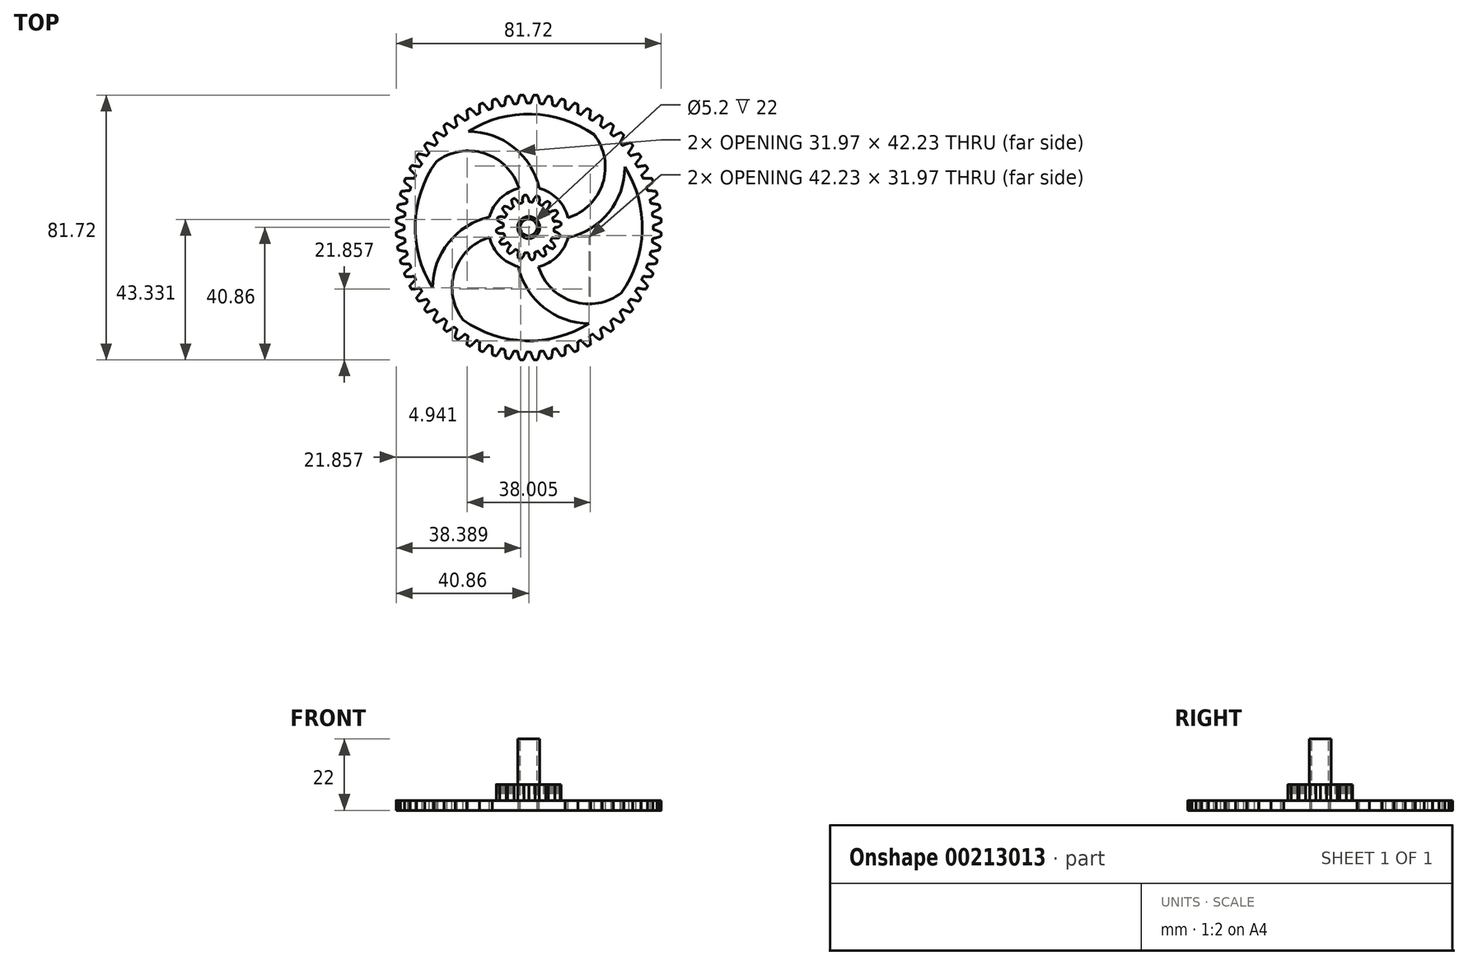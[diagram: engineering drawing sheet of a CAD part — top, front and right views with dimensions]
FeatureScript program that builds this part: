
annotation { "Feature Type Name" : "Feature", "Feature Type Description" : "" }
export const myFeature = defineFeature(function(context is Context, id is Id, definition is map)
    precondition{}
    {
        {
            var Q0;
            Q0=qCreatedBy(makeId("Top.planeOp"),FACE);
            var sketch = newSketch(context, id + "F0", { "sketchPlane" : qUnion([Q0])});
            skCircle(sketch, "E0", {"center": v(0, 0) * mm, "radius": 37.31 * mm, "construction": true});
            skLineSegment(sketch, "E1", {"start": v(0, 0) * mm, "end": v(37.31, 0) * mm, "construction": true});
            skLineSegment(sketch, "E2", {"start": v(37.31, 0) * mm, "end": v(37.31, 0) * mm});
            skLineSegment(sketch, "E3", {"start": v(0, 0) * mm, "end": v(37.27, 1.7) * mm, "construction": true});
            skLineSegment(sketch, "E4", {"start": v(37.27, 1.7) * mm, "end": v(37.35, 0) * mm, "construction": true});
            skLineSegment(sketch, "E5", {"start": v(0, 0) * mm, "end": v(37.16, 3.38) * mm, "construction": true});
            skLineSegment(sketch, "E6", {"start": v(37.16, 3.38) * mm, "end": v(37.46, 0) * mm, "construction": true});
            skLineSegment(sketch, "E7", {"start": v(0, 0) * mm, "end": v(36.97, 5.06) * mm, "construction": true});
            skLineSegment(sketch, "E8", {"start": v(36.97, 5.06) * mm, "end": v(37.66, 0.03) * mm, "construction": true});
            skLineSegment(sketch, "E9", {"start": v(0, 0) * mm, "end": v(36.7, 6.74) * mm, "construction": true});
            skLineSegment(sketch, "E10", {"start": v(36.7, 6.74) * mm, "end": v(37.92, 0.07) * mm, "construction": true});
            skLineSegment(sketch, "E11", {"start": v(0, 0) * mm, "end": v(36.36, 8.4) * mm, "construction": true});
            skLineSegment(sketch, "E12", {"start": v(36.36, 8.4) * mm, "end": v(38.26, 0.14) * mm, "construction": true});
            skLineSegment(sketch, "E13", {"start": v(0, 0) * mm, "end": v(35.94, 10.03) * mm, "construction": true});
            skLineSegment(sketch, "E14", {"start": v(35.94, 10.03) * mm, "end": v(38.67, 0.25) * mm, "construction": true});
            skLineSegment(sketch, "E15", {"start": v(0, 0) * mm, "end": v(35.44, 11.65) * mm, "construction": true});
            skLineSegment(sketch, "E16", {"start": v(35.44, 11.65) * mm, "end": v(39.15, 0.4) * mm, "construction": true});
            skLineSegment(sketch, "E17", {"start": v(0, 0) * mm, "end": v(34.88, 13.25) * mm, "construction": true});
            skLineSegment(sketch, "E18", {"start": v(34.88, 13.25) * mm, "end": v(39.69, 0.59) * mm, "construction": true});
            skLineSegment(sketch, "E19", {"start": v(0, 0) * mm, "end": v(34.24, 14.82) * mm, "construction": true});
            skLineSegment(sketch, "E20", {"start": v(34.24, 14.82) * mm, "end": v(40.3, 0.83) * mm, "construction": true});
            skLineSegment(sketch, "E21", {"start": v(0, 0) * mm, "end": v(33.54, 16.36) * mm, "construction": true});
            skLineSegment(sketch, "E22", {"start": v(33.54, 16.36) * mm, "end": v(40.96, 1.14) * mm, "construction": true});
            skPoint(sketch, "E23", {"position": v(37.31, 0) * mm});
            skCircle(sketch, "E24", {"center": v(0, 0) * mm, "radius": 38.38 * mm});
            skFitSpline(sketch, "E25", {"points": [v(37.31, 0) * mm, v(37.35, 0) * mm, v(37.46, 0) * mm, v(37.66, 0.03) * mm, v(37.92, 0.07) * mm, v(38.26, 0.14) * mm, v(38.67, 0.25) * mm, v(39.15, 0.4) * mm, v(39.69, 0.59) * mm, v(40.3, 0.83) * mm, v(40.96, 1.14) * mm], "startDerivative": vector(1, 0.02) * mm, "endDerivative": vector(4.58, 2.16) * mm, "construction": true});
            skFitSpline(sketch, "E26", {"points": [v(37.31, 0) * mm, v(37.35, 0) * mm, v(37.46, 0) * mm, v(37.66, 0.03) * mm, v(37.92, 0.07) * mm, v(38.26, 0.14) * mm, v(38.67, 0.25) * mm, v(39.15, 0.4) * mm, v(39.69, 0.59) * mm, v(40.3, 0.83) * mm, v(40.96, 1.14) * mm], "startDerivative": vector(1, 0.02) * mm, "endDerivative": vector(4.58, 2.16) * mm});
            skLineSegment(sketch, "E27", {"start": v(0, 0) * mm, "end": v(51.74, 2.13) * mm, "construction": true});
            skFitSpline(sketch, "E28.MirrorCS", {"points": [v(37.19, 3.06) * mm, v(37.22, 3.06) * mm, v(37.34, 3.07) * mm, v(37.53, 3.06) * mm, v(37.8, 3.04) * mm, v(38.14, 3) * mm, v(38.56, 2.93) * mm, v(39.05, 2.82) * mm, v(39.6, 2.67) * mm, v(40.23, 2.48) * mm, v(40.91, 2.23) * mm], "startDerivative": vector(1, 0.06) * mm, "endDerivative": vector(4.74, -1.78) * mm});
            skArc(sketch, "E29", {"start": v(40.83, 2.26) * mm, "mid": v(-40.86, -1.68) * mm, "end": v(40.88, 1.1) * mm, "construction": true});
            skArc(sketch, "E30", {"start": v(40.88, 1.1) * mm, "mid": v(40.86, 1.68) * mm, "end": v(40.83, 2.26) * mm});
            skSolve(sketch);
        }
        {
            var Q0;
            Q0=qCreatedBy(makeId("Front.planeOp"),FACE);
            var sketch = newSketch(context, id + "F1", { "sketchPlane" : qUnion([Q0])});
            skLineSegment(sketch, "E31", {"start": v(0, 0) * mm, "end": v(0, 52.01) * mm});
            skSolve(sketch);
        }
        {
            var Q0;
            {var subQ0=sQuery(id+"F0.wireOp",EDGE,"E24");var subQ1=makeQuery(id+"F0.imprint","INTERSECT",VERTEX,{"derivedFrom":[subQ0,sQuery(id+"F0.wireOp",EDGE,"E26")]});Q0=makeQuery(id+"F0.imprint","IMPRINT",FACE,{"disambiguationData":[TD([[makeQuery(id+"F0.imprint","IMPRINT",EDGE,{"disambiguationData":[TD([[subQ1,-1.0]])],"derivedFrom":subQ0}),1.0]])]});}
            var Q1;
            {var subQ0=sQuery(id+"F0.wireOp",EDGE,"E26");Q1=makeQuery(id+"F0.imprint","IMPRINT",FACE,{"disambiguationData":[TD([[makeQuery(id+"F0.imprint","IMPRINT",EDGE,{"derivedFrom":subQ0}),1.0]])]});}
            extrude(context, id + "F2", {"entities" : qUnion([Q0, Q1]), "depth" : 3 * mm});
        }
        {
            var Q0;
            Q0=makeQuery(id+"F2.opExtrude","SWEPT_EDGE",EDGE,{"disambiguationData":[OSD([sQuery(id+"F0.wireOp",EDGE,"E24"),sQuery(id+"F0.wireOp",EDGE,"E26")])]});
            var Q1;
            Q1=makeQuery(id+"F2.opExtrude","SWEPT_EDGE",EDGE,{"disambiguationData":[OSD([sQuery(id+"F0.wireOp",EDGE,"E26"),sQuery(id+"F0.wireOp",EDGE,"E30")])]});
            var Q2;
            Q2=makeQuery(id+"F2.opExtrude","SWEPT_EDGE",EDGE,{"disambiguationData":[OSD([sQuery(id+"F0.wireOp",EDGE,"E28.MirrorCS"),sQuery(id+"F0.wireOp",EDGE,"E30")])]});
            var Q3;
            Q3=makeQuery(id+"F2.opExtrude","SWEPT_EDGE",EDGE,{"disambiguationData":[OSD([sQuery(id+"F0.wireOp",EDGE,"E24"),sQuery(id+"F0.wireOp",EDGE,"E28.MirrorCS")])]});
            fillet(context, id + "F3", {"entities" : qUnion([Q0, Q1, Q2, Q3]), "radius" : 0.3 * mm, "tangentPropagation" : true, "allowEdgeOverflow" : false});
        }
        {
            var Q0;
            Q0=makeQuery(id+"F2.opExtrude","SWEPT_BODY",BODY,{"disambiguationData":[OSD([sQuery(id+"F0.wireOp",EDGE,"E24"),sQuery(id+"F0.wireOp",EDGE,"E26"),sQuery(id+"F0.wireOp",EDGE,"E28.MirrorCS"),sQuery(id+"F0.wireOp",EDGE,"E30")])]});
            var Q1;
            Q1=sQuery(id+"F1.wireOp",EDGE,"E31");
            circularPattern(context, id + "F4", {"operationType" : NewBodyOperationType.ADD, "entities" : qUnion([Q0]), "axis" : qUnion([Q1]), "angle" : 360 * degree, "instanceCount" : 60, "equalSpace" : true});
        }
        {
            var Q0;
            {var subQ0=makeQuery(id+"F2.opExtrude","CAP_FACE",FACE,{"disambiguationData":[OSD([sQuery(id+"F0.wireOp",EDGE,"E24"),sQuery(id+"F0.wireOp",EDGE,"E26"),sQuery(id+"F0.wireOp",EDGE,"E28.MirrorCS"),sQuery(id+"F0.wireOp",EDGE,"E30")])],"isStart":false});Q0=makeQuery(id+"F4.boolean.opBoolean","MERGE",FACE,{"derivedFrom":[subQ0,makeQuery(id+"F4.opPattern","COPY",FACE,{"derivedFrom":subQ0,"instanceName":"1"}),makeQuery(id+"F4.opPattern","COPY",FACE,{"derivedFrom":subQ0,"instanceName":"2"}),makeQuery(id+"F4.opPattern","COPY",FACE,{"derivedFrom":subQ0,"instanceName":"3"}),makeQuery(id+"F4.opPattern","COPY",FACE,{"derivedFrom":subQ0,"instanceName":"4"}),makeQuery(id+"F4.opPattern","COPY",FACE,{"derivedFrom":subQ0,"instanceName":"5"}),makeQuery(id+"F4.opPattern","COPY",FACE,{"derivedFrom":subQ0,"instanceName":"6"}),makeQuery(id+"F4.opPattern","COPY",FACE,{"derivedFrom":subQ0,"instanceName":"7"}),makeQuery(id+"F4.opPattern","COPY",FACE,{"derivedFrom":subQ0,"instanceName":"8"}),makeQuery(id+"F4.opPattern","COPY",FACE,{"derivedFrom":subQ0,"instanceName":"9"}),makeQuery(id+"F4.opPattern","COPY",FACE,{"derivedFrom":subQ0,"instanceName":"10"}),makeQuery(id+"F4.opPattern","COPY",FACE,{"derivedFrom":subQ0,"instanceName":"11"}),makeQuery(id+"F4.opPattern","COPY",FACE,{"derivedFrom":subQ0,"instanceName":"12"}),makeQuery(id+"F4.opPattern","COPY",FACE,{"derivedFrom":subQ0,"instanceName":"13"}),makeQuery(id+"F4.opPattern","COPY",FACE,{"derivedFrom":subQ0,"instanceName":"14"}),makeQuery(id+"F4.opPattern","COPY",FACE,{"derivedFrom":subQ0,"instanceName":"15"}),makeQuery(id+"F4.opPattern","COPY",FACE,{"derivedFrom":subQ0,"instanceName":"16"}),makeQuery(id+"F4.opPattern","COPY",FACE,{"derivedFrom":subQ0,"instanceName":"17"}),makeQuery(id+"F4.opPattern","COPY",FACE,{"derivedFrom":subQ0,"instanceName":"18"}),makeQuery(id+"F4.opPattern","COPY",FACE,{"derivedFrom":subQ0,"instanceName":"19"}),makeQuery(id+"F4.opPattern","COPY",FACE,{"derivedFrom":subQ0,"instanceName":"20"}),makeQuery(id+"F4.opPattern","COPY",FACE,{"derivedFrom":subQ0,"instanceName":"21"}),makeQuery(id+"F4.opPattern","COPY",FACE,{"derivedFrom":subQ0,"instanceName":"22"}),makeQuery(id+"F4.opPattern","COPY",FACE,{"derivedFrom":subQ0,"instanceName":"23"}),makeQuery(id+"F4.opPattern","COPY",FACE,{"derivedFrom":subQ0,"instanceName":"24"}),makeQuery(id+"F4.opPattern","COPY",FACE,{"derivedFrom":subQ0,"instanceName":"25"}),makeQuery(id+"F4.opPattern","COPY",FACE,{"derivedFrom":subQ0,"instanceName":"26"}),makeQuery(id+"F4.opPattern","COPY",FACE,{"derivedFrom":subQ0,"instanceName":"27"}),makeQuery(id+"F4.opPattern","COPY",FACE,{"derivedFrom":subQ0,"instanceName":"28"}),makeQuery(id+"F4.opPattern","COPY",FACE,{"derivedFrom":subQ0,"instanceName":"29"}),makeQuery(id+"F4.opPattern","COPY",FACE,{"derivedFrom":subQ0,"instanceName":"30"}),makeQuery(id+"F4.opPattern","COPY",FACE,{"derivedFrom":subQ0,"instanceName":"31"}),makeQuery(id+"F4.opPattern","COPY",FACE,{"derivedFrom":subQ0,"instanceName":"32"}),makeQuery(id+"F4.opPattern","COPY",FACE,{"derivedFrom":subQ0,"instanceName":"33"}),makeQuery(id+"F4.opPattern","COPY",FACE,{"derivedFrom":subQ0,"instanceName":"34"}),makeQuery(id+"F4.opPattern","COPY",FACE,{"derivedFrom":subQ0,"instanceName":"35"}),makeQuery(id+"F4.opPattern","COPY",FACE,{"derivedFrom":subQ0,"instanceName":"36"}),makeQuery(id+"F4.opPattern","COPY",FACE,{"derivedFrom":subQ0,"instanceName":"37"}),makeQuery(id+"F4.opPattern","COPY",FACE,{"derivedFrom":subQ0,"instanceName":"38"}),makeQuery(id+"F4.opPattern","COPY",FACE,{"derivedFrom":subQ0,"instanceName":"39"}),makeQuery(id+"F4.opPattern","COPY",FACE,{"derivedFrom":subQ0,"instanceName":"40"}),makeQuery(id+"F4.opPattern","COPY",FACE,{"derivedFrom":subQ0,"instanceName":"41"}),makeQuery(id+"F4.opPattern","COPY",FACE,{"derivedFrom":subQ0,"instanceName":"42"}),makeQuery(id+"F4.opPattern","COPY",FACE,{"derivedFrom":subQ0,"instanceName":"43"}),makeQuery(id+"F4.opPattern","COPY",FACE,{"derivedFrom":subQ0,"instanceName":"44"}),makeQuery(id+"F4.opPattern","COPY",FACE,{"derivedFrom":subQ0,"instanceName":"45"}),makeQuery(id+"F4.opPattern","COPY",FACE,{"derivedFrom":subQ0,"instanceName":"46"}),makeQuery(id+"F4.opPattern","COPY",FACE,{"derivedFrom":subQ0,"instanceName":"47"}),makeQuery(id+"F4.opPattern","COPY",FACE,{"derivedFrom":subQ0,"instanceName":"48"}),makeQuery(id+"F4.opPattern","COPY",FACE,{"derivedFrom":subQ0,"instanceName":"49"}),makeQuery(id+"F4.opPattern","COPY",FACE,{"derivedFrom":subQ0,"instanceName":"50"}),makeQuery(id+"F4.opPattern","COPY",FACE,{"derivedFrom":subQ0,"instanceName":"51"}),makeQuery(id+"F4.opPattern","COPY",FACE,{"derivedFrom":subQ0,"instanceName":"52"}),makeQuery(id+"F4.opPattern","COPY",FACE,{"derivedFrom":subQ0,"instanceName":"53"}),makeQuery(id+"F4.opPattern","COPY",FACE,{"derivedFrom":subQ0,"instanceName":"54"}),makeQuery(id+"F4.opPattern","COPY",FACE,{"derivedFrom":subQ0,"instanceName":"55"}),makeQuery(id+"F4.opPattern","COPY",FACE,{"derivedFrom":subQ0,"instanceName":"56"}),makeQuery(id+"F4.opPattern","COPY",FACE,{"derivedFrom":subQ0,"instanceName":"57"}),makeQuery(id+"F4.opPattern","COPY",FACE,{"derivedFrom":subQ0,"instanceName":"58"}),makeQuery(id+"F4.opPattern","COPY",FACE,{"derivedFrom":subQ0,"instanceName":"59"})]});}
            var sketch = newSketch(context, id + "F5", { "sketchPlane" : qUnion([Q0])});
            skLineSegment(sketch, "E32", {"start": v(0, 0) * mm, "end": v(38.38, -0.43) * mm, "construction": true});
            skCircle(sketch, "E33", {"center": v(0, 0) * mm, "radius": 8.46 * mm, "construction": true});
            skLineSegment(sketch, "E34", {"start": v(7.68, 4.49) * mm, "end": v(7.68, 4.49) * mm});
            skLineSegment(sketch, "E35", {"start": v(0, 0) * mm, "end": v(8.44, 0.55) * mm, "construction": true});
            skLineSegment(sketch, "E36", {"start": v(8.44, 0.55) * mm, "end": v(8.47, 0) * mm, "construction": true});
            skLineSegment(sketch, "E37", {"start": v(0, 0) * mm, "end": v(8.39, 1.09) * mm, "construction": true});
            skLineSegment(sketch, "E38", {"start": v(8.39, 1.09) * mm, "end": v(8.53, 0) * mm, "construction": true});
            skLineSegment(sketch, "E39", {"start": v(0, 0) * mm, "end": v(8.3, 1.63) * mm, "construction": true});
            skLineSegment(sketch, "E40", {"start": v(8.3, 1.63) * mm, "end": v(8.61, 0.02) * mm, "construction": true});
            skLineSegment(sketch, "E41", {"start": v(0, 0) * mm, "end": v(8.18, 2.16) * mm, "construction": true});
            skLineSegment(sketch, "E42", {"start": v(8.18, 2.16) * mm, "end": v(8.73, 0.05) * mm, "construction": true});
            skLineSegment(sketch, "E43", {"start": v(0, 0) * mm, "end": v(8.02, 2.68) * mm, "construction": true});
            skLineSegment(sketch, "E44", {"start": v(8.02, 2.68) * mm, "end": v(8.89, 0.1) * mm, "construction": true});
            skLineSegment(sketch, "E45", {"start": v(0, 0) * mm, "end": v(7.83, 3.2) * mm, "construction": true});
            skLineSegment(sketch, "E46", {"start": v(7.83, 3.2) * mm, "end": v(9.07, 0.16) * mm, "construction": true});
            skLineSegment(sketch, "E47", {"start": v(0, 0) * mm, "end": v(7.6, 3.7) * mm, "construction": true});
            skLineSegment(sketch, "E48", {"start": v(7.6, 3.7) * mm, "end": v(9.28, 0.26) * mm, "construction": true});
            skLineSegment(sketch, "E49", {"start": v(0, 0) * mm, "end": v(7.35, 4.18) * mm, "construction": true});
            skLineSegment(sketch, "E50", {"start": v(7.35, 4.18) * mm, "end": v(9.51, 0.38) * mm, "construction": true});
            skLineSegment(sketch, "E51", {"start": v(0, 0) * mm, "end": v(7.07, 4.64) * mm, "construction": true});
            skLineSegment(sketch, "E52", {"start": v(7.07, 4.64) * mm, "end": v(9.77, 0.53) * mm, "construction": true});
            skLineSegment(sketch, "E53", {"start": v(0, 0) * mm, "end": v(6.75, 5.09) * mm, "construction": true});
            skLineSegment(sketch, "E54", {"start": v(6.75, 5.09) * mm, "end": v(10.04, 0.73) * mm, "construction": true});
            skPoint(sketch, "E55", {"position": v(8.46, 0) * mm});
            skCircle(sketch, "E56", {"center": v(0, 0) * mm, "radius": 7.87 * mm});
            skLineSegment(sketch, "E57", {"start": v(7.87, 0) * mm, "end": v(8.46, 0) * mm});
            skFitSpline(sketch, "E58", {"points": [v(8.46, 0) * mm, v(8.47, 0) * mm, v(8.53, 0) * mm, v(8.61, 0.02) * mm, v(8.73, 0.05) * mm, v(8.89, 0.1) * mm, v(9.07, 0.16) * mm, v(9.28, 0.26) * mm, v(9.51, 0.38) * mm, v(9.77, 0.53) * mm, v(10.04, 0.73) * mm], "startDerivative": vector(0.46, 0.01) * mm, "endDerivative": vector(1.88, 1.36) * mm});
            skFitSpline(sketch, "E59", {"points": [v(8.46, 0) * mm, v(8.47, 0) * mm, v(8.53, 0) * mm, v(8.61, 0.02) * mm, v(8.73, 0.05) * mm, v(8.89, 0.1) * mm, v(9.07, 0.16) * mm, v(9.28, 0.26) * mm, v(9.51, 0.38) * mm, v(9.77, 0.53) * mm, v(10.04, 0.73) * mm], "startDerivative": vector(0.46, 0.01) * mm, "endDerivative": vector(1.88, 1.36) * mm, "construction": true});
            skLineSegment(sketch, "E60", {"start": v(0, 0) * mm, "end": v(11.88, 1.35) * mm, "construction": true});
            skLineSegment(sketch, "E61.MirrorCS", {"start": v(7.67, 1.77) * mm, "end": v(8.24, 1.9) * mm});
            skFitSpline(sketch, "E62.MirrorCS", {"points": [v(8.24, 1.9) * mm, v(8.26, 1.9) * mm, v(8.31, 1.9) * mm, v(8.4, 1.91) * mm, v(8.52, 1.91) * mm, v(8.68, 1.9) * mm, v(8.87, 1.88) * mm, v(9.1, 1.83) * mm, v(9.35, 1.76) * mm, v(9.64, 1.67) * mm, v(9.95, 1.54) * mm], "startDerivative": vector(0.45, 0.1) * mm, "endDerivative": vector(2.14, -0.9) * mm});
            skArc(sketch, "E63", {"start": v(9.89, 1.57) * mm, "mid": v(-9.95, -1.13) * mm, "end": v(9.99, 0.7) * mm, "construction": true});
            skArc(sketch, "E64", {"start": v(9.99, 0.7) * mm, "mid": v(9.95, 1.13) * mm, "end": v(9.89, 1.57) * mm});
            skSolve(sketch);
        }
        {
            var Q0;
            Q0=makeQuery(id+"F2.opExtrude","SWEPT_BODY",BODY,{"disambiguationData":[OSD([sQuery(id+"F0.wireOp",EDGE,"E24"),sQuery(id+"F0.wireOp",EDGE,"E26"),sQuery(id+"F0.wireOp",EDGE,"E28.MirrorCS"),sQuery(id+"F0.wireOp",EDGE,"E30")])]});
            var Q1;
            Q1=sQuery(id+"F1.wireOp",EDGE,"E31");
            transform(context, id + "F6", {"entities" : qUnion([Q0]), "transformType" : TransformType.ROTATION, "transformAxis" : qUnion([Q1]), "angle" : 0.65 * degree, "makeCopy" : false});
        }
        {
            var Q0;
            {var subQ0=sQuery(id+"F5.wireOp",EDGE,"E56");var subQ1=makeQuery(id+"F5.imprint","INTERSECT",VERTEX,{"derivedFrom":[subQ0,sQuery(id+"F5.wireOp",EDGE,"E57")]});Q0=makeQuery(id+"F5.imprint","IMPRINT",FACE,{"disambiguationData":[TD([[makeQuery(id+"F5.imprint","IMPRINT",EDGE,{"disambiguationData":[TD([[subQ1,-1.0]])],"derivedFrom":subQ0}),1.0]])]});}
            var Q1;
            {var subQ1=sQuery(id+"F5.wireOp",EDGE,"E57");Q1=makeQuery(id+"F5.imprint","IMPRINT",FACE,{"disambiguationData":[TD([[makeQuery(id+"F5.imprint","IMPRINT",EDGE,{"derivedFrom":subQ1}),1.0]])]});}
            extrude(context, id + "F7", {"entities" : qUnion([Q0, Q1]), "depth" : 5 * mm});
        }
        {
            var Q0;
            Q0=makeQuery(id+"F7.opExtrude","SWEPT_EDGE",EDGE,{"disambiguationData":[OSD([sQuery(id+"F5.wireOp",EDGE,"E56"),sQuery(id+"F5.wireOp",EDGE,"E57")])]});
            var Q1;
            Q1=makeQuery(id+"F7.opExtrude","SWEPT_EDGE",EDGE,{"disambiguationData":[OSD([sQuery(id+"F5.wireOp",EDGE,"E58"),sQuery(id+"F5.wireOp",EDGE,"E64")])]});
            var Q2;
            Q2=makeQuery(id+"F7.opExtrude","SWEPT_EDGE",EDGE,{"disambiguationData":[OSD([sQuery(id+"F5.wireOp",EDGE,"E62.MirrorCS"),sQuery(id+"F5.wireOp",EDGE,"E64")])]});
            var Q3;
            Q3=makeQuery(id+"F7.opExtrude","SWEPT_EDGE",EDGE,{"disambiguationData":[OSD([sQuery(id+"F5.wireOp",EDGE,"E56"),sQuery(id+"F5.wireOp",EDGE,"E61.MirrorCS")])]});
            fillet(context, id + "F8", {"entities" : qUnion([Q0, Q1, Q2, Q3]), "radius" : 0.3 * mm, "tangentPropagation" : true, "allowEdgeOverflow" : false});
        }
        {
            var Q0;
            Q0=makeQuery(id+"F7.opExtrude","SWEPT_BODY",BODY,{"disambiguationData":[OSD([sQuery(id+"F5.wireOp",EDGE,"E56"),sQuery(id+"F5.wireOp",EDGE,"E57"),sQuery(id+"F5.wireOp",EDGE,"E58"),sQuery(id+"F5.wireOp",EDGE,"E61.MirrorCS"),sQuery(id+"F5.wireOp",EDGE,"E62.MirrorCS"),sQuery(id+"F5.wireOp",EDGE,"E64")])]});
            var Q1;
            Q1=sQuery(id+"F1.wireOp",EDGE,"E31");
            circularPattern(context, id + "F9", {"operationType" : NewBodyOperationType.ADD, "entities" : qUnion([Q0]), "axis" : qUnion([Q1]), "angle" : 360 * degree, "instanceCount" : 16, "equalSpace" : true});
        }
        {
            var Q0;
            {var subQ0=makeQuery(id+"F7.opExtrude","CAP_FACE",FACE,{"disambiguationData":[OSD([sQuery(id+"F5.wireOp",EDGE,"E56"),sQuery(id+"F5.wireOp",EDGE,"E57"),sQuery(id+"F5.wireOp",EDGE,"E58"),sQuery(id+"F5.wireOp",EDGE,"E61.MirrorCS"),sQuery(id+"F5.wireOp",EDGE,"E62.MirrorCS"),sQuery(id+"F5.wireOp",EDGE,"E64")])],"isStart":false});Q0=makeQuery(id+"F9.boolean.opBoolean","MERGE",FACE,{"derivedFrom":[subQ0,makeQuery(id+"F9.opPattern","COPY",FACE,{"derivedFrom":subQ0,"instanceName":"1"}),makeQuery(id+"F9.opPattern","COPY",FACE,{"derivedFrom":subQ0,"instanceName":"2"}),makeQuery(id+"F9.opPattern","COPY",FACE,{"derivedFrom":subQ0,"instanceName":"3"}),makeQuery(id+"F9.opPattern","COPY",FACE,{"derivedFrom":subQ0,"instanceName":"4"}),makeQuery(id+"F9.opPattern","COPY",FACE,{"derivedFrom":subQ0,"instanceName":"5"}),makeQuery(id+"F9.opPattern","COPY",FACE,{"derivedFrom":subQ0,"instanceName":"6"}),makeQuery(id+"F9.opPattern","COPY",FACE,{"derivedFrom":subQ0,"instanceName":"7"}),makeQuery(id+"F9.opPattern","COPY",FACE,{"derivedFrom":subQ0,"instanceName":"8"}),makeQuery(id+"F9.opPattern","COPY",FACE,{"derivedFrom":subQ0,"instanceName":"9"}),makeQuery(id+"F9.opPattern","COPY",FACE,{"derivedFrom":subQ0,"instanceName":"10"}),makeQuery(id+"F9.opPattern","COPY",FACE,{"derivedFrom":subQ0,"instanceName":"11"}),makeQuery(id+"F9.opPattern","COPY",FACE,{"derivedFrom":subQ0,"instanceName":"12"}),makeQuery(id+"F9.opPattern","COPY",FACE,{"derivedFrom":subQ0,"instanceName":"13"}),makeQuery(id+"F9.opPattern","COPY",FACE,{"derivedFrom":subQ0,"instanceName":"14"}),makeQuery(id+"F9.opPattern","COPY",FACE,{"derivedFrom":subQ0,"instanceName":"15"})]});}
            var sketch = newSketch(context, id + "F10", { "sketchPlane" : qUnion([Q0])});
            skCircle(sketch, "E65", {"center": v(0, 0) * mm, "radius": 3.4 * mm});
            skSolve(sketch);
        }
        {
            var Q0;
            Q0=makeQuery(id+"F10.imprint","IMPRINT",FACE,{"disambiguationData":[TD([[makeQuery(id+"F10.imprint","IMPRINT",EDGE,{"derivedFrom":sQuery(id+"F10.wireOp",EDGE,"E65")}),1.0]])]});
            extrude(context, id + "F11", {"entities" : qUnion([Q0]), "operationType" : NewBodyOperationType.ADD, "depth" : 14 * mm});
        }
        {
            var Q0;
            Q0=makeQuery(id+"F11.opExtrude","CAP_FACE",FACE,{"disambiguationData":[OSD([sQuery(id+"F10.wireOp",EDGE,"E65")])],"isStart":false});
            var sketch = newSketch(context, id + "F12", { "sketchPlane" : qUnion([Q0])});
            skCircle(sketch, "E66", {"center": v(0, 0) * mm, "radius": 2.6 * mm});
            skSolve(sketch);
        }
        {
            var Q0;
            Q0=makeQuery(id+"F12.imprint","IMPRINT",FACE,{"disambiguationData":[TD([[makeQuery(id+"F12.imprint","IMPRINT",EDGE,{"derivedFrom":sQuery(id+"F12.wireOp",EDGE,"E66")}),1.0]])]});
            extrude(context, id + "F13", {"entities" : qUnion([Q0]), "operationType" : NewBodyOperationType.REMOVE, "endBound" : BoundingType.UP_TO_NEXT, "oppositeDirection" : true, "depth" : 25 * mm});
        }
        {
            var Q0;
            {var subQ71=sQuery(id+"F5.wireOp",EDGE,"E57");Q0=makeQuery(id+"F5.imprint","IMPRINT",FACE,{"disambiguationData":[TD([[makeQuery(id+"F5.imprint","IMPRINT",EDGE,{"derivedFrom":subQ71}),-1.0]])]});}
            var sketch = newSketch(context, id + "F14", { "sketchPlane" : qUnion([Q0])});
            skCircle(sketch, "E67", {"center": v(0, 0) * mm, "radius": 12.5 * mm});
            skCircle(sketch, "E68", {"center": v(0, 0) * mm, "radius": 35 * mm});
            skLineSegment(sketch, "E69", {"start": v(0, 0) * mm, "end": v(-23.42, 26.01) * mm, "construction": true});
            skCircle(sketch, "E70", {"center": v(-18.6, 7.3) * mm, "radius": 19.31 * mm, "construction": true});
            skPoint(sketch, "E70.first.point", {"position": v(0, 12.5) * mm});
            skPoint(sketch, "E70.third.point", {"position": v(-8.59, 23.82) * mm});
            skArc(sketch, "E71", {"start": v(3.2, 12.09) * mm, "mid": v(-4.63, 24.7) * mm, "end": v(-18.64, 29.62) * mm});
            skArc(sketch, "E72", {"start": v(-3.02, 12.13) * mm, "mid": v(-13.68, 22.86) * mm, "end": v(-28.57, 20.22) * mm});
            skArc(sketch, "E73.1.0", {"start": v(-12.09, 3.2) * mm, "mid": v(-24.7, -4.63) * mm, "end": v(-29.62, -18.64) * mm});
            skArc(sketch, "E73.1.1", {"start": v(-12.13, -3.02) * mm, "mid": v(-22.86, -13.68) * mm, "end": v(-20.22, -28.57) * mm});
            skArc(sketch, "E73.2.0", {"start": v(-3.2, -12.09) * mm, "mid": v(4.63, -24.7) * mm, "end": v(18.64, -29.62) * mm});
            skArc(sketch, "E73.2.1", {"start": v(3.02, -12.13) * mm, "mid": v(13.68, -22.86) * mm, "end": v(28.57, -20.22) * mm});
            skArc(sketch, "E73.3.0", {"start": v(12.09, -3.2) * mm, "mid": v(24.7, 4.63) * mm, "end": v(29.62, 18.64) * mm});
            skArc(sketch, "E73.3.1", {"start": v(12.13, 3.02) * mm, "mid": v(22.86, 13.68) * mm, "end": v(20.22, 28.57) * mm});
            skSolve(sketch);
        }
        {
            var Q0;
            {var subQ0=sQuery(id+"F14.wireOp",EDGE,"E73.1.1");Q0=makeQuery(id+"F14.imprint","IMPRINT",FACE,{"disambiguationData":[TD([[makeQuery(id+"F14.imprint","IMPRINT",EDGE,{"derivedFrom":subQ0}),1.0]])]});}
            var Q1;
            {var subQ0=sQuery(id+"F14.wireOp",EDGE,"E72");Q1=makeQuery(id+"F14.imprint","IMPRINT",FACE,{"disambiguationData":[TD([[makeQuery(id+"F14.imprint","IMPRINT",EDGE,{"derivedFrom":subQ0}),1.0]])]});}
            var Q2;
            {var subQ0=sQuery(id+"F14.wireOp",EDGE,"E73.2.1");Q2=makeQuery(id+"F14.imprint","IMPRINT",FACE,{"disambiguationData":[TD([[makeQuery(id+"F14.imprint","IMPRINT",EDGE,{"derivedFrom":subQ0}),1.0]])]});}
            var Q3;
            {var subQ0=sQuery(id+"F14.wireOp",EDGE,"E71");Q3=makeQuery(id+"F14.imprint","IMPRINT",FACE,{"disambiguationData":[TD([[makeQuery(id+"F14.imprint","IMPRINT",EDGE,{"derivedFrom":subQ0}),-1.0]])]});}
            extrude(context, id + "F15", {"entities" : qUnion([Q0, Q1, Q2, Q3]), "operationType" : NewBodyOperationType.REMOVE, "endBound" : BoundingType.UP_TO_NEXT, "oppositeDirection" : true, "depth" : 25 * mm});
        }
    });
